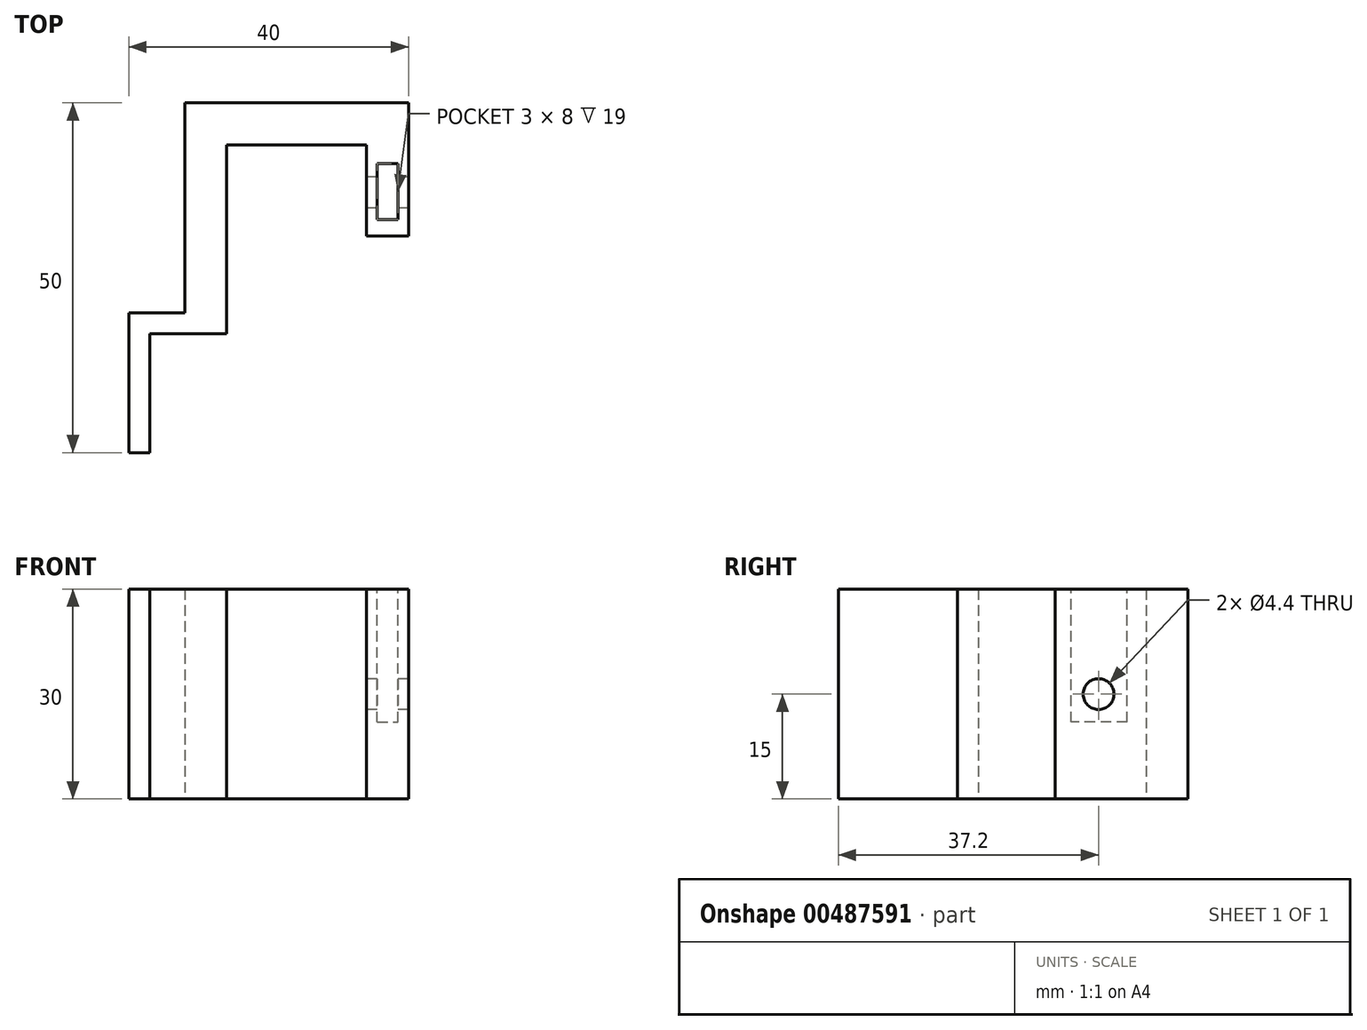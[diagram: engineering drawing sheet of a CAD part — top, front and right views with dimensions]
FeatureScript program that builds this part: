
annotation { "Feature Type Name" : "Feature", "Feature Type Description" : "" }
export const myFeature = defineFeature(function(context is Context, id is Id, definition is map)
    precondition{}
    {
        {
            assignVariable(context, id + "F0", {"variableType" : VariableType.LENGTH, "name" : "BracketDepth", "lengthValue" : 30 * mm});
        }
        {
            assignVariable(context, id + "F1", {"variableType" : VariableType.LENGTH, "name" : "SquareNutWidth", "lengthValue" : 8 * mm});
        }
        {
            var Q0;
            Q0=qCreatedBy(makeId("Top.planeOp"),FACE);
            var sketch = newSketch(context, id + "F2", { "sketchPlane" : qUnion([Q0])});
            skLineSegment(sketch, "E0", {"start": v(0, 0) * mm, "end": v(0, 13) * mm});
            skLineSegment(sketch, "E1", {"start": v(0, 13) * mm, "end": v(-20, 13) * mm});
            skLineSegment(sketch, "E2", {"start": v(-20, 13) * mm, "end": v(-20, -14) * mm});
            skLineSegment(sketch, "E3", {"start": v(-20, -14) * mm, "end": v(-31, -14) * mm});
            skLineSegment(sketch, "E4", {"start": v(-31, -14) * mm, "end": v(-31, -31) * mm});
            skLineSegment(sketch, "E5", {"start": v(0, 0) * mm, "end": v(6, 0) * mm});
            skLineSegment(sketch, "E6", {"start": v(6, 0) * mm, "end": v(6, 19) * mm});
            skLineSegment(sketch, "E7", {"start": v(6, 19) * mm, "end": v(-26, 19) * mm});
            skLineSegment(sketch, "E8", {"start": v(-26, 19) * mm, "end": v(-26, -11) * mm});
            skLineSegment(sketch, "E9", {"start": v(-26, -11) * mm, "end": v(-34, -11) * mm});
            skLineSegment(sketch, "E10", {"start": v(-34, -11) * mm, "end": v(-34, -31) * mm});
            skLineSegment(sketch, "E11", {"start": v(-34, -31) * mm, "end": v(-31, -31) * mm});
            skSolve(sketch);
        }
        {
            var Q0;
            Q0 = qSketchRegion(id + "F2", true);
            extrude(context, id + "F3", {"entities" : qUnion([Q0]), "offsetDistance" : 25 * mm, "depth" : getVariable(context, 'BracketDepth')});
        }
        {
            var Q0;
            Q0=makeQuery(id+"F3.opExtrude","SWEPT_FACE",FACE,{"disambiguationData":[OSD([sQuery(id+"F2.wireOp",EDGE,"E0")])]});
            var sketch = newSketch(context, id + "F4", { "sketchPlane" : qUnion([Q0])});
            skCircle(sketch, "E12", {"center": v(-6.2, 15) * mm, "radius": 2.2 * mm});
            skPoint(sketch, "E12.centerSnap0", {"position": v(0, 15) * mm});
            skSolve(sketch);
        }
        {
            var Q0;
            Q0=makeQuery(id+"F4.imprint","IMPRINT",FACE,{"disambiguationData":[TD([[makeQuery(id+"F4.imprint","IMPRINT",EDGE,{"derivedFrom":sQuery(id+"F4.wireOp",EDGE,"E12")}),1.0]])]});
            extrude(context, id + "F5", {"entities" : qUnion([Q0]), "operationType" : NewBodyOperationType.REMOVE, "oppositeDirection" : true, "depth" : 6 * mm, "offsetDistance" : 25 * mm});
        }
        {
            var Q0;
            Q0=makeQuery(id+"F3.opExtrude","CAP_FACE",FACE,{"disambiguationData":[OSD([sQuery(id+"F2.wireOp",EDGE,"E0"),sQuery(id+"F2.wireOp",EDGE,"E1"),sQuery(id+"F2.wireOp",EDGE,"E2"),sQuery(id+"F2.wireOp",EDGE,"E3"),sQuery(id+"F2.wireOp",EDGE,"E4"),sQuery(id+"F2.wireOp",EDGE,"E5"),sQuery(id+"F2.wireOp",EDGE,"E6"),sQuery(id+"F2.wireOp",EDGE,"E7"),sQuery(id+"F2.wireOp",EDGE,"E8"),sQuery(id+"F2.wireOp",EDGE,"E9"),sQuery(id+"F2.wireOp",EDGE,"E10"),sQuery(id+"F2.wireOp",EDGE,"E11")])],"isStart":false});
            var sketch = newSketch(context, id + "F6", { "sketchPlane" : qUnion([Q0])});
            skLineSegment(sketch, "E13.bottom", {"start": v(1.5, 10.3) * mm, "end": v(4.5, 10.3) * mm});
            skLineSegment(sketch, "E13.top", {"start": v(1.5, 2.3) * mm, "end": v(4.5, 2.3) * mm});
            skLineSegment(sketch, "E13.left", {"start": v(1.5, 10.3) * mm, "end": v(1.5, 2.3) * mm});
            skLineSegment(sketch, "E13.right", {"start": v(4.5, 10.3) * mm, "end": v(4.5, 2.3) * mm});
            skPoint(sketch, "E13.middle", {"position": v(3, 6.3) * mm});
            skSolve(sketch);
        }
        {
            var Q0;
            Q0 = qSketchRegion(id + "F6", true);
            extrude(context, id + "F7", {"entities" : qUnion([Q0]), "operationType" : NewBodyOperationType.REMOVE, "oppositeDirection" : true, "depth" : getVariable(context, 'BracketDepth') - ((getVariable(context, 'BracketDepth') - getVariable(context, 'SquareNutWidth')) / 2), "offsetDistance" : 25 * mm});
        }
    });
